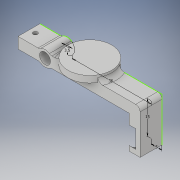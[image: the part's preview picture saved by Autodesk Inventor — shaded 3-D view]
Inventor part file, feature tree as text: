
AUTODESK INVENTOR PART (.ipt)
format: ipt  version: 2019 (Build 230136000, 136)  size: 164,352 bytes
history: native  units: in
note: dims shown in document units (in); Inventor stores cm internally (conversion verified against a paired STEP export)
features: fillet x7, sketch x4, extrude x3, hole x1
ambient origin geometry x8: Origin, YZ Plane, XZ Plane, XY Plane, X Axis, Y Axis, Z Axis, Center Point
bodies: Solid1 (feature_tree)
feature tree (15):
  sketch  "Sketch1"  dims[d6=0.1969in d7=0.1378in]
  extrude  "Extrusion1"  Depth=0.1378in
  extrude  "Extrusion2"  Depth=0.5906in
  fillet  "Fillet1"  Radius=0.1969in
  fillet  "Fillet2"  Radius=0.3937in
  fillet  "Fillet3"  Radius=0.7874in
  extrude  "Extrusion3"  Depth=0.0787in
  fillet  "Fillet4"  Radius=0.0787in
  fillet  "Fillet5"  Radius=0.0787in
  fillet  "Fillet6"  Radius=0.1181in
  fillet  "Fillet7"  Radius=0.0787in
  hole  "Hole2"  [1 undecoded]
  sketch  "Sketch2"  dims[d8=1.4173in d9=0.5906in d10=0.1969in d14=0.3937in d15=0.0in d16=0.7874in]
  sketch  "Sketch3"  dims[d17=0.1181in d18=0.0in d19=0.0787in d20=0.0787in d21=0.0787in d22=0.1181in d23=0.0in d24=0.0787in]
  sketch  "Sketch5"  dims[d25=0.0787in d26=0.0787in d27=0.0787in d35=0.0787in d36=0.2362in d37=0.1575in d38=0.0787in d39=90.0deg d40=0.0787in d41=0.0in]
note: 1 required parameter value undecoded (feature->parameter linkage not recoverable at this tier; creation-order binding heuristic only, values carry confidence <= 0.55)
